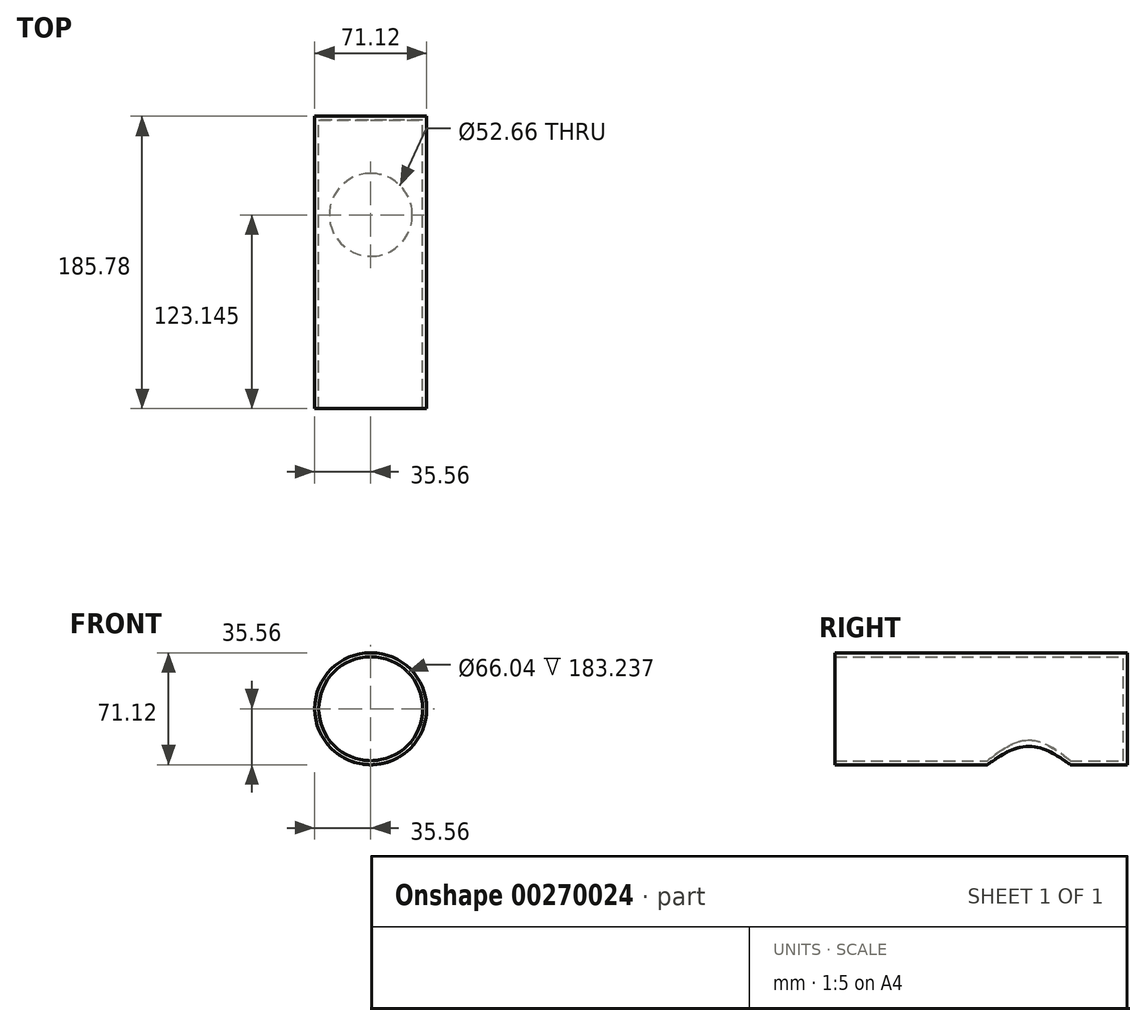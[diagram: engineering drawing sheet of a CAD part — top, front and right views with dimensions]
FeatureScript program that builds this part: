
annotation { "Feature Type Name" : "Feature", "Feature Type Description" : "" }
export const myFeature = defineFeature(function(context is Context, id is Id, definition is map)
    precondition{}
    {
        {
            var Q0;
            Q0=qCreatedBy(makeId("Front.planeOp"),FACE);
            var sketch = newSketch(context, id + "F0", { "sketchPlane" : qUnion([Q0])});
            skCircle(sketch, "E0", {"center": v(0, 0) * mm, "radius": 35.56 * mm});
            skSolve(sketch);
        }
        {
            var Q0;
            Q0=makeQuery(id+"F0.imprint","IMPRINT",FACE,{"disambiguationData":[TD([[makeQuery(id+"F0.imprint","IMPRINT",EDGE,{"derivedFrom":sQuery(id+"F0.wireOp",EDGE,"E0")}),1.0]])]});
            extrude(context, id + "F1", {"entities" : qUnion([Q0]), "depth" : 185.78 * mm});
        }
        {
            var Q0;
            Q0=makeQuery(id+"F1.opExtrude","CAP_FACE",FACE,{"disambiguationData":[OSD([sQuery(id+"F0.wireOp",EDGE,"E0")])],"isStart":false});
            shell(context, id + "F2", {"entities" : qUnion([Q0]), "thickness" : 2.54 * mm});
        }
        {
            var Q0;
            Q0=qCreatedBy(makeId("Top.planeOp"),FACE);
            var sketch = newSketch(context, id + "F3", { "sketchPlane" : qUnion([Q0])});
            skCircle(sketch, "E1", {"center": v(0, -62.63) * mm, "radius": 26.33 * mm});
            skSolve(sketch);
        }
        {
            var Q0;
            Q0 = qSketchRegion(id + "F3", true);
            extrude(context, id + "F4", {"entities" : qUnion([Q0]), "operationType" : NewBodyOperationType.REMOVE, "oppositeDirection" : true, "depth" : 101.88 * mm});
        }
    });
